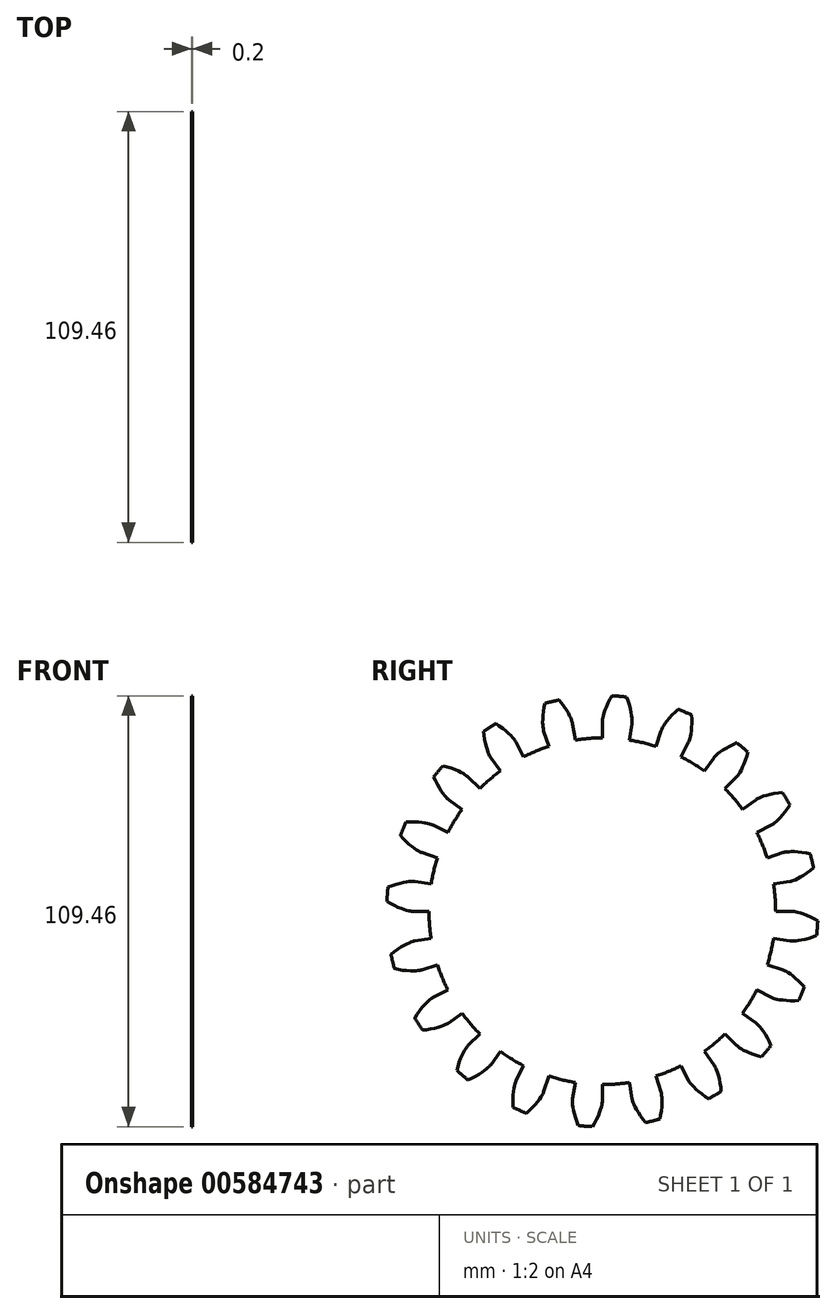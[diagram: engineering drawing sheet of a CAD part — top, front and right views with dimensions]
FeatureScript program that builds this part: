
annotation { "Feature Type Name" : "Feature", "Feature Type Description" : "" }
export const myFeature = defineFeature(function(context is Context, id is Id, definition is map)
    precondition{}
    {
        {
            assignVariable(context, id + "F0", {"name" : "GearThickness", "anyValue" : .2});
        }
        {
            var Q0;
            Q0=qCreatedBy(makeId("Right.planeOp"),FACE);
            var sketch = newSketch(context, id + "F1", { "sketchPlane" : qUnion([Q0])});
            skCircle(sketch, "E0", {"center": v(0, 0) * mm, "radius": 44.04 * mm});
            skCircle(sketch, "E1", {"center": v(0, 0) * mm, "radius": 48.22 * mm, "construction": true});
            skCircle(sketch, "E2", {"center": v(0, 0) * mm, "radius": 49.8 * mm, "construction": true});
            skCircle(sketch, "E3", {"center": v(0, 0) * mm, "radius": 54.78 * mm});
            skLineSegment(sketch, "E4", {"start": v(0, 0) * mm, "end": v(-48.22, 0) * mm, "construction": true});
            skLineSegment(sketch, "E5.1.0", {"start": v(0, 0) * mm, "end": v(-48.16, 2.4) * mm, "construction": true});
            skLineSegment(sketch, "E5.2.0", {"start": v(0, 0) * mm, "end": v(-47.98, 4.81) * mm, "construction": true});
            skLineSegment(sketch, "E5.3.0", {"start": v(0, 0) * mm, "end": v(-47.68, 7.2) * mm, "construction": true});
            skLineSegment(sketch, "E5.4.0", {"start": v(0, 0) * mm, "end": v(-47.26, 9.58) * mm, "construction": true});
            skLineSegment(sketch, "E5.5.0", {"start": v(0, 0) * mm, "end": v(-46.72, 11.93) * mm, "construction": true});
            skLineSegment(sketch, "E5.6.0", {"start": v(0, 0) * mm, "end": v(-46.06, 14.25) * mm, "construction": true});
            skLineSegment(sketch, "E5.7.0", {"start": v(0, 0) * mm, "end": v(-45.3, 16.53) * mm, "construction": true});
            skLineSegment(sketch, "E5.8.0", {"start": v(0, 0) * mm, "end": v(-44.41, 18.78) * mm, "construction": true});
            skLineSegment(sketch, "E5.9.0", {"start": v(0, 0) * mm, "end": v(-43.42, 20.97) * mm, "construction": true});
            skLineSegment(sketch, "E5.10.0", {"start": v(0, 0) * mm, "end": v(-42.31, 23.12) * mm, "construction": true});
            skLineSegment(sketch, "E5.11.0", {"start": v(0, 0) * mm, "end": v(-41.1, 25.2) * mm, "construction": true});
            skLineSegment(sketch, "E5.12.0", {"start": v(0, 0) * mm, "end": v(-39.8, 27.23) * mm, "construction": true});
            skLineSegment(sketch, "E5.13.0", {"start": v(0, 0) * mm, "end": v(-38.39, 29.18) * mm, "construction": true});
            skLineSegment(sketch, "E5.14.0", {"start": v(0, 0) * mm, "end": v(-36.88, 31.06) * mm, "construction": true});
            skLineSegment(sketch, "E5.anchor2", {"start": v(0, 0) * mm, "end": v(-36.88, 31.06) * mm, "construction": true});
            skLineSegment(sketch, "E6", {"start": v(-48.16, 2.4) * mm, "end": v(-48.28, 0) * mm, "construction": true});
            skLineSegment(sketch, "E7", {"start": v(-47.98, 4.81) * mm, "end": v(-48.46, 0.02) * mm, "construction": true});
            skLineSegment(sketch, "E8", {"start": v(-47.68, 7.2) * mm, "end": v(-48.76, 0.05) * mm, "construction": true});
            skLineSegment(sketch, "E9", {"start": v(-46.72, 11.93) * mm, "end": v(-49.7, 0.25) * mm, "construction": true});
            skLineSegment(sketch, "E10", {"start": v(-46.06, 14.25) * mm, "end": v(-50.34, 0.43) * mm, "construction": true});
            skLineSegment(sketch, "E11", {"start": v(-45.3, 16.53) * mm, "end": v(-51.08, 0.68) * mm, "construction": true});
            skLineSegment(sketch, "E12", {"start": v(-44.41, 18.78) * mm, "end": v(-51.92, 1.01) * mm, "construction": true});
            skLineSegment(sketch, "E13", {"start": v(-43.42, 20.97) * mm, "end": v(-52.86, 1.44) * mm, "construction": true});
            skLineSegment(sketch, "E14", {"start": v(-42.31, 23.12) * mm, "end": v(-53.87, 1.96) * mm, "construction": true});
            skLineSegment(sketch, "E15", {"start": v(-41.1, 25.2) * mm, "end": v(-54.97, 2.6) * mm, "construction": true});
            skLineSegment(sketch, "E16", {"start": v(-47.26, 9.58) * mm, "end": v(-49.17, 0.13) * mm, "construction": true});
            skLineSegment(sketch, "E17", {"start": v(-39.8, 27.23) * mm, "end": v(-56.13, 3.35) * mm, "construction": true});
            skLineSegment(sketch, "E18", {"start": v(-38.39, 29.18) * mm, "end": v(-57.35, 4.23) * mm, "construction": true});
            skLineSegment(sketch, "E19", {"start": v(-36.88, 31.06) * mm, "end": v(-58.62, 5.25) * mm, "construction": true});
            skLineSegment(sketch, "E20", {"start": v(0, 0) * mm, "end": v(-48.07, 3.78) * mm, "construction": true});
            skLineSegment(sketch, "E21", {"start": v(-44.04, 0) * mm, "end": v(-48.22, 0) * mm});
            skLineSegment(sketch, "E22.MirrorCS", {"start": v(-43.5, 6.89) * mm, "end": v(-47.62, 7.54) * mm});
            skLineSegment(sketch, "E23", {"start": v(-48.22, 0) * mm, "end": v(-48.28, 0) * mm});
            skLineSegment(sketch, "E24", {"start": v(-48.28, 0) * mm, "end": v(-48.46, 0.02) * mm});
            skLineSegment(sketch, "E25", {"start": v(-48.46, 0.02) * mm, "end": v(-48.76, 0.05) * mm});
            skLineSegment(sketch, "E26", {"start": v(-48.76, 0.05) * mm, "end": v(-49.17, 0.13) * mm});
            skLineSegment(sketch, "E27", {"start": v(-49.17, 0.13) * mm, "end": v(-49.7, 0.25) * mm});
            skLineSegment(sketch, "E28", {"start": v(-49.7, 0.25) * mm, "end": v(-50.34, 0.43) * mm});
            skLineSegment(sketch, "E29", {"start": v(-50.34, 0.43) * mm, "end": v(-51.08, 0.68) * mm});
            skLineSegment(sketch, "E30", {"start": v(-51.08, 0.68) * mm, "end": v(-51.92, 1.01) * mm});
            skLineSegment(sketch, "E31", {"start": v(-51.92, 1.01) * mm, "end": v(-52.86, 1.44) * mm});
            skLineSegment(sketch, "E32", {"start": v(-52.86, 1.44) * mm, "end": v(-53.87, 1.96) * mm});
            skLineSegment(sketch, "E33", {"start": v(-53.87, 1.96) * mm, "end": v(-54.97, 2.6) * mm});
            skLineSegment(sketch, "E34", {"start": v(-54.97, 2.6) * mm, "end": v(-56.13, 3.35) * mm});
            skLineSegment(sketch, "E35", {"start": v(-56.13, 3.35) * mm, "end": v(-57.35, 4.23) * mm});
            skLineSegment(sketch, "E36", {"start": v(-57.35, 4.23) * mm, "end": v(-58.62, 5.25) * mm});
            skLineSegment(sketch, "E37.MirrorCS", {"start": v(-47.62, 7.54) * mm, "end": v(-47.68, 7.55) * mm});
            skLineSegment(sketch, "E38.MirrorCS", {"start": v(-47.68, 7.55) * mm, "end": v(-47.86, 7.56) * mm});
            skLineSegment(sketch, "E39.MirrorCS", {"start": v(-47.86, 7.56) * mm, "end": v(-48.17, 7.57) * mm});
            skLineSegment(sketch, "E40.MirrorCS", {"start": v(-48.17, 7.57) * mm, "end": v(-48.59, 7.57) * mm});
            skLineSegment(sketch, "E41.MirrorCS", {"start": v(-49.13, 7.53) * mm, "end": v(-49.79, 7.45) * mm});
            skLineSegment(sketch, "E42.MirrorCS", {"start": v(-49.79, 7.45) * mm, "end": v(-50.56, 7.32) * mm});
            skLineSegment(sketch, "E43.MirrorCS", {"start": v(-50.56, 7.32) * mm, "end": v(-51.44, 7.12) * mm});
            skLineSegment(sketch, "E44.MirrorCS", {"start": v(-51.44, 7.12) * mm, "end": v(-52.43, 6.85) * mm});
            skLineSegment(sketch, "E45.MirrorCS", {"start": v(-53.52, 6.5) * mm, "end": v(-54.7, 6.04) * mm});
            skLineSegment(sketch, "E46.MirrorCS", {"start": v(-52.43, 6.85) * mm, "end": v(-53.52, 6.5) * mm});
            skLineSegment(sketch, "E47.MirrorCS", {"start": v(-54.7, 6.04) * mm, "end": v(-55.96, 5.47) * mm});
            skLineSegment(sketch, "E48.MirrorCS", {"start": v(-55.96, 5.47) * mm, "end": v(-57.3, 4.8) * mm});
            skLineSegment(sketch, "E49.MirrorCS", {"start": v(-57.3, 4.8) * mm, "end": v(-58.72, 3.99) * mm});
            skLineSegment(sketch, "E50.MirrorCS", {"start": v(-48.59, 7.57) * mm, "end": v(-49.13, 7.53) * mm});
            skLineSegment(sketch, "E51.1.0", {"start": v(-41.89, -13.6) * mm, "end": v(-45.86, -14.9) * mm});
            skLineSegment(sketch, "E51.1.1", {"start": v(-53.89, -11.16) * mm, "end": v(-54.92, -12.09) * mm});
            skLineSegment(sketch, "E51.1.2", {"start": v(-43.5, -6.89) * mm, "end": v(-47.62, -7.54) * mm});
            skLineSegment(sketch, "E51.1.3", {"start": v(-52.9, -10.36) * mm, "end": v(-53.89, -11.16) * mm});
            skLineSegment(sketch, "E51.1.4", {"start": v(-51.84, -14.78) * mm, "end": v(-53.08, -14.52) * mm});
            skLineSegment(sketch, "E51.1.5", {"start": v(-53.08, -14.52) * mm, "end": v(-54.42, -14.16) * mm});
            skLineSegment(sketch, "E51.1.6", {"start": v(-51.98, -9.69) * mm, "end": v(-52.9, -10.36) * mm});
            skLineSegment(sketch, "E51.1.7", {"start": v(-55.98, -13.15) * mm, "end": v(-57.08, -14.35) * mm});
            skLineSegment(sketch, "E51.1.8", {"start": v(-51.12, -9.12) * mm, "end": v(-51.98, -9.69) * mm});
            skLineSegment(sketch, "E51.1.9", {"start": v(-55.85, -13.7) * mm, "end": v(-57.37, -13.12) * mm});
            skLineSegment(sketch, "E51.1.10", {"start": v(-54.92, -12.09) * mm, "end": v(-55.98, -13.15) * mm});
            skLineSegment(sketch, "E51.1.11", {"start": v(-50.71, -14.97) * mm, "end": v(-51.84, -14.78) * mm});
            skLineSegment(sketch, "E51.1.12", {"start": v(-54.42, -14.16) * mm, "end": v(-55.85, -13.7) * mm});
            skLineSegment(sketch, "E51.1.13", {"start": v(-49.05, -8.02) * mm, "end": v(-49.65, -8.3) * mm});
            skLineSegment(sketch, "E51.1.14", {"start": v(-49.65, -8.3) * mm, "end": v(-50.35, -8.66) * mm});
            skLineSegment(sketch, "E51.1.15", {"start": v(-50.35, -8.66) * mm, "end": v(-51.12, -9.12) * mm});
            skLineSegment(sketch, "E51.1.16", {"start": v(-48.8, -15.14) * mm, "end": v(-49.7, -15.08) * mm});
            skLineSegment(sketch, "E51.1.17", {"start": v(-48, -15.15) * mm, "end": v(-48.8, -15.14) * mm});
            skLineSegment(sketch, "E51.1.18", {"start": v(-49.7, -15.08) * mm, "end": v(-50.71, -14.97) * mm});
            skLineSegment(sketch, "E51.1.19", {"start": v(-48.55, -7.82) * mm, "end": v(-49.05, -8.02) * mm});
            skLineSegment(sketch, "E51.1.20", {"start": v(-48.15, -7.68) * mm, "end": v(-48.55, -7.82) * mm});
            skLineSegment(sketch, "E51.1.21", {"start": v(-47.35, -15.12) * mm, "end": v(-48, -15.15) * mm});
            skLineSegment(sketch, "E51.1.22", {"start": v(-46.8, -15.07) * mm, "end": v(-47.35, -15.12) * mm});
            skLineSegment(sketch, "E51.1.23", {"start": v(-46.1, -14.96) * mm, "end": v(-46.39, -15.02) * mm});
            skLineSegment(sketch, "E51.1.24", {"start": v(-47.62, -7.54) * mm, "end": v(-47.68, -7.55) * mm});
            skLineSegment(sketch, "E51.1.25", {"start": v(-47.68, -7.55) * mm, "end": v(-47.86, -7.6) * mm});
            skLineSegment(sketch, "E51.1.26", {"start": v(-46.39, -15.02) * mm, "end": v(-46.8, -15.07) * mm});
            skLineSegment(sketch, "E51.1.27", {"start": v(-47.86, -7.6) * mm, "end": v(-48.15, -7.68) * mm});
            skLineSegment(sketch, "E51.1.28", {"start": v(-45.92, -14.92) * mm, "end": v(-46.1, -14.96) * mm});
            skLineSegment(sketch, "E51.1.29", {"start": v(-45.86, -14.9) * mm, "end": v(-45.92, -14.92) * mm});
            skLineSegment(sketch, "E51.2.0", {"start": v(-35.63, -25.89) * mm, "end": v(-39, -28.34) * mm});
            skLineSegment(sketch, "E51.2.1", {"start": v(-47.8, -27.27) * mm, "end": v(-48.5, -28.47) * mm});
            skLineSegment(sketch, "E51.2.2", {"start": v(-39.24, -20) * mm, "end": v(-42.96, -21.9) * mm});
            skLineSegment(sketch, "E51.2.3", {"start": v(-47.11, -26.2) * mm, "end": v(-47.8, -27.27) * mm});
            skLineSegment(sketch, "E51.2.4", {"start": v(-44.74, -30.08) * mm, "end": v(-46, -30.21) * mm});
            skLineSegment(sketch, "E51.2.5", {"start": v(-46, -30.21) * mm, "end": v(-47.38, -30.28) * mm});
            skLineSegment(sketch, "E51.2.6", {"start": v(-46.44, -25.27) * mm, "end": v(-47.11, -26.2) * mm});
            skLineSegment(sketch, "E51.2.7", {"start": v(-49.18, -29.8) * mm, "end": v(-49.85, -31.29) * mm});
            skLineSegment(sketch, "E51.2.8", {"start": v(-45.8, -24.47) * mm, "end": v(-46.44, -25.27) * mm});
            skLineSegment(sketch, "E51.2.9", {"start": v(-48.89, -30.29) * mm, "end": v(-50.51, -30.21) * mm});
            skLineSegment(sketch, "E51.2.10", {"start": v(-48.5, -28.47) * mm, "end": v(-49.18, -29.8) * mm});
            skLineSegment(sketch, "E51.2.11", {"start": v(-43.6, -29.9) * mm, "end": v(-44.74, -30.08) * mm});
            skLineSegment(sketch, "E51.2.12", {"start": v(-47.38, -30.28) * mm, "end": v(-48.89, -30.29) * mm});
            skLineSegment(sketch, "E51.2.13", {"start": v(-44.17, -22.79) * mm, "end": v(-44.66, -23.24) * mm});
            skLineSegment(sketch, "E51.2.14", {"start": v(-44.66, -23.24) * mm, "end": v(-45.2, -23.8) * mm});
            skLineSegment(sketch, "E51.2.15", {"start": v(-45.2, -23.8) * mm, "end": v(-45.8, -24.47) * mm});
            skLineSegment(sketch, "E51.2.16", {"start": v(-41.73, -29.47) * mm, "end": v(-42.6, -29.7) * mm});
            skLineSegment(sketch, "E51.2.17", {"start": v(-40.98, -29.24) * mm, "end": v(-41.73, -29.47) * mm});
            skLineSegment(sketch, "E51.2.18", {"start": v(-42.6, -29.7) * mm, "end": v(-43.6, -29.9) * mm});
            skLineSegment(sketch, "E51.2.19", {"start": v(-43.75, -22.44) * mm, "end": v(-44.17, -22.79) * mm});
            skLineSegment(sketch, "E51.2.20", {"start": v(-43.42, -22.18) * mm, "end": v(-43.75, -22.44) * mm});
            skLineSegment(sketch, "E51.2.21", {"start": v(-40.36, -29.01) * mm, "end": v(-40.98, -29.24) * mm});
            skLineSegment(sketch, "E51.2.22", {"start": v(-39.86, -28.8) * mm, "end": v(-40.36, -29.01) * mm});
            skLineSegment(sketch, "E51.2.23", {"start": v(-39.21, -28.47) * mm, "end": v(-39.48, -28.61) * mm});
            skLineSegment(sketch, "E51.2.24", {"start": v(-42.96, -21.9) * mm, "end": v(-43.01, -21.92) * mm});
            skLineSegment(sketch, "E51.2.25", {"start": v(-43.01, -21.92) * mm, "end": v(-43.17, -22.01) * mm});
            skLineSegment(sketch, "E51.2.26", {"start": v(-39.48, -28.61) * mm, "end": v(-39.86, -28.8) * mm});
            skLineSegment(sketch, "E51.2.27", {"start": v(-43.17, -22.01) * mm, "end": v(-43.42, -22.18) * mm});
            skLineSegment(sketch, "E51.2.28", {"start": v(-39.06, -28.38) * mm, "end": v(-39.21, -28.47) * mm});
            skLineSegment(sketch, "E51.2.29", {"start": v(-39, -28.34) * mm, "end": v(-39.06, -28.38) * mm});
            skLineSegment(sketch, "E51.3.0", {"start": v(-25.89, -35.63) * mm, "end": v(-28.34, -39) * mm});
            skLineSegment(sketch, "E51.3.1", {"start": v(-37.03, -40.7) * mm, "end": v(-37.32, -42.06) * mm});
            skLineSegment(sketch, "E51.3.2", {"start": v(-31.14, -31.14) * mm, "end": v(-34.1, -34.1) * mm});
            skLineSegment(sketch, "E51.3.3", {"start": v(-36.7, -39.48) * mm, "end": v(-37.03, -40.7) * mm});
            skLineSegment(sketch, "E51.3.4", {"start": v(-33.25, -42.43) * mm, "end": v(-34.4, -42.95) * mm});
            skLineSegment(sketch, "E51.3.5", {"start": v(-34.4, -42.95) * mm, "end": v(-35.7, -43.44) * mm});
            skLineSegment(sketch, "E51.3.6", {"start": v(-36.36, -38.39) * mm, "end": v(-36.7, -39.48) * mm});
            skLineSegment(sketch, "E51.3.7", {"start": v(-37.56, -43.55) * mm, "end": v(-37.74, -45.16) * mm});
            skLineSegment(sketch, "E51.3.8", {"start": v(-36, -37.43) * mm, "end": v(-36.36, -38.39) * mm});
            skLineSegment(sketch, "E51.3.9", {"start": v(-37.13, -43.91) * mm, "end": v(-38.7, -44.34) * mm});
            skLineSegment(sketch, "E51.3.10", {"start": v(-37.32, -42.06) * mm, "end": v(-37.56, -43.55) * mm});
            skLineSegment(sketch, "E51.3.11", {"start": v(-32.23, -41.92) * mm, "end": v(-33.25, -42.43) * mm});
            skLineSegment(sketch, "E51.3.12", {"start": v(-35.7, -43.44) * mm, "end": v(-37.13, -43.91) * mm});
            skLineSegment(sketch, "E51.3.13", {"start": v(-34.97, -35.32) * mm, "end": v(-35.3, -35.9) * mm});
            skLineSegment(sketch, "E51.3.14", {"start": v(-35.3, -35.9) * mm, "end": v(-35.64, -36.6) * mm});
            skLineSegment(sketch, "E51.3.15", {"start": v(-35.64, -36.6) * mm, "end": v(-36, -37.43) * mm});
            skLineSegment(sketch, "E51.3.16", {"start": v(-30.58, -40.93) * mm, "end": v(-31.34, -41.41) * mm});
            skLineSegment(sketch, "E51.3.17", {"start": v(-29.94, -40.47) * mm, "end": v(-30.58, -40.93) * mm});
            skLineSegment(sketch, "E51.3.18", {"start": v(-31.34, -41.41) * mm, "end": v(-32.23, -41.92) * mm});
            skLineSegment(sketch, "E51.3.19", {"start": v(-34.68, -34.86) * mm, "end": v(-34.97, -35.32) * mm});
            skLineSegment(sketch, "E51.3.20", {"start": v(-34.44, -34.51) * mm, "end": v(-34.68, -34.86) * mm});
            skLineSegment(sketch, "E51.3.21", {"start": v(-29.42, -40.06) * mm, "end": v(-29.94, -40.47) * mm});
            skLineSegment(sketch, "E51.3.22", {"start": v(-29, -39.7) * mm, "end": v(-29.42, -40.06) * mm});
            skLineSegment(sketch, "E51.3.23", {"start": v(-28.5, -39.2) * mm, "end": v(-28.7, -39.41) * mm});
            skLineSegment(sketch, "E51.3.24", {"start": v(-34.1, -34.1) * mm, "end": v(-34.14, -34.14) * mm});
            skLineSegment(sketch, "E51.3.25", {"start": v(-34.14, -34.14) * mm, "end": v(-34.25, -34.28) * mm});
            skLineSegment(sketch, "E51.3.26", {"start": v(-28.7, -39.41) * mm, "end": v(-29, -39.7) * mm});
            skLineSegment(sketch, "E51.3.27", {"start": v(-34.25, -34.28) * mm, "end": v(-34.44, -34.51) * mm});
            skLineSegment(sketch, "E51.3.28", {"start": v(-28.38, -39.06) * mm, "end": v(-28.5, -39.2) * mm});
            skLineSegment(sketch, "E51.3.29", {"start": v(-28.34, -39) * mm, "end": v(-28.38, -39.06) * mm});
            skLineSegment(sketch, "E51.4.0", {"start": v(-13.6, -41.89) * mm, "end": v(-14.9, -45.86) * mm});
            skLineSegment(sketch, "E51.4.1", {"start": v(-22.64, -50.15) * mm, "end": v(-22.5, -51.53) * mm});
            skLineSegment(sketch, "E51.4.2", {"start": v(-20, -39.24) * mm, "end": v(-21.9, -42.96) * mm});
            skLineSegment(sketch, "E51.4.3", {"start": v(-22.71, -48.9) * mm, "end": v(-22.64, -50.15) * mm});
            skLineSegment(sketch, "E51.4.4", {"start": v(-18.51, -50.63) * mm, "end": v(-19.45, -51.48) * mm});
            skLineSegment(sketch, "E51.4.5", {"start": v(-19.45, -51.48) * mm, "end": v(-20.53, -52.35) * mm});
            skLineSegment(sketch, "E51.4.6", {"start": v(-22.72, -47.75) * mm, "end": v(-22.71, -48.9) * mm});
            skLineSegment(sketch, "E51.4.7", {"start": v(-22.27, -53.02) * mm, "end": v(-21.94, -54.62) * mm});
            skLineSegment(sketch, "E51.4.8", {"start": v(-22.67, -46.72) * mm, "end": v(-22.72, -47.75) * mm});
            skLineSegment(sketch, "E51.4.9", {"start": v(-21.75, -53.24) * mm, "end": v(-23.1, -54.13) * mm});
            skLineSegment(sketch, "E51.4.10", {"start": v(-22.5, -51.53) * mm, "end": v(-22.27, -53.02) * mm});
            skLineSegment(sketch, "E51.4.11", {"start": v(-17.7, -49.82) * mm, "end": v(-18.51, -50.63) * mm});
            skLineSegment(sketch, "E51.4.12", {"start": v(-20.53, -52.35) * mm, "end": v(-21.75, -53.24) * mm});
            skLineSegment(sketch, "E51.4.13", {"start": v(-22.34, -44.4) * mm, "end": v(-22.47, -45.05) * mm});
            skLineSegment(sketch, "E51.4.14", {"start": v(-22.47, -45.05) * mm, "end": v(-22.58, -45.82) * mm});
            skLineSegment(sketch, "E51.4.15", {"start": v(-22.58, -45.82) * mm, "end": v(-22.67, -46.72) * mm});
            skLineSegment(sketch, "E51.4.16", {"start": v(-16.43, -48.37) * mm, "end": v(-17, -49.07) * mm});
            skLineSegment(sketch, "E51.4.17", {"start": v(-15.96, -47.74) * mm, "end": v(-16.43, -48.37) * mm});
            skLineSegment(sketch, "E51.4.18", {"start": v(-17, -49.07) * mm, "end": v(-17.7, -49.82) * mm});
            skLineSegment(sketch, "E51.4.19", {"start": v(-22.2, -43.87) * mm, "end": v(-22.34, -44.4) * mm});
            skLineSegment(sketch, "E51.4.20", {"start": v(-22.09, -43.47) * mm, "end": v(-22.2, -43.87) * mm});
            skLineSegment(sketch, "E51.4.21", {"start": v(-15.6, -47.2) * mm, "end": v(-15.96, -47.74) * mm});
            skLineSegment(sketch, "E51.4.22", {"start": v(-15.32, -46.73) * mm, "end": v(-15.6, -47.2) * mm});
            skLineSegment(sketch, "E51.4.23", {"start": v(-14.99, -46.08) * mm, "end": v(-15.12, -46.35) * mm});
            skLineSegment(sketch, "E51.4.24", {"start": v(-21.9, -42.96) * mm, "end": v(-21.92, -43.02) * mm});
            skLineSegment(sketch, "E51.4.25", {"start": v(-21.92, -43.02) * mm, "end": v(-21.99, -43.18) * mm});
            skLineSegment(sketch, "E51.4.26", {"start": v(-15.12, -46.35) * mm, "end": v(-15.32, -46.73) * mm});
            skLineSegment(sketch, "E51.4.27", {"start": v(-21.99, -43.18) * mm, "end": v(-22.09, -43.47) * mm});
            skLineSegment(sketch, "E51.4.28", {"start": v(-14.92, -45.91) * mm, "end": v(-14.99, -46.08) * mm});
            skLineSegment(sketch, "E51.4.29", {"start": v(-14.9, -45.86) * mm, "end": v(-14.92, -45.91) * mm});
            skLineSegment(sketch, "E51.5.0", {"start": v(0, -44.04) * mm, "end": v(0, -48.22) * mm});
            skLineSegment(sketch, "E51.5.1", {"start": v(-6.04, -54.7) * mm, "end": v(-5.47, -55.96) * mm});
            skLineSegment(sketch, "E51.5.2", {"start": v(-6.89, -43.5) * mm, "end": v(-7.54, -47.62) * mm});
            skLineSegment(sketch, "E51.5.3", {"start": v(-6.5, -53.52) * mm, "end": v(-6.04, -54.7) * mm});
            skLineSegment(sketch, "E51.5.4", {"start": v(-1.96, -53.87) * mm, "end": v(-2.6, -54.97) * mm});
            skLineSegment(sketch, "E51.5.5", {"start": v(-2.6, -54.97) * mm, "end": v(-3.35, -56.13) * mm});
            skLineSegment(sketch, "E51.5.6", {"start": v(-6.85, -52.43) * mm, "end": v(-6.5, -53.52) * mm});
            skLineSegment(sketch, "E51.5.7", {"start": v(-4.8, -57.3) * mm, "end": v(-3.99, -58.72) * mm});
            skLineSegment(sketch, "E51.5.8", {"start": v(-7.12, -51.44) * mm, "end": v(-6.85, -52.43) * mm});
            skLineSegment(sketch, "E51.5.9", {"start": v(-4.23, -57.35) * mm, "end": v(-5.25, -58.62) * mm});
            skLineSegment(sketch, "E51.5.10", {"start": v(-5.47, -55.96) * mm, "end": v(-4.8, -57.3) * mm});
            skLineSegment(sketch, "E51.5.11", {"start": v(-1.44, -52.86) * mm, "end": v(-1.96, -53.87) * mm});
            skLineSegment(sketch, "E51.5.12", {"start": v(-3.35, -56.13) * mm, "end": v(-4.23, -57.35) * mm});
            skLineSegment(sketch, "E51.5.13", {"start": v(-7.53, -49.13) * mm, "end": v(-7.45, -49.79) * mm});
            skLineSegment(sketch, "E51.5.14", {"start": v(-7.45, -49.79) * mm, "end": v(-7.32, -50.56) * mm});
            skLineSegment(sketch, "E51.5.15", {"start": v(-7.32, -50.56) * mm, "end": v(-7.12, -51.44) * mm});
            skLineSegment(sketch, "E51.5.16", {"start": v(-0.68, -51.08) * mm, "end": v(-1.01, -51.92) * mm});
            skLineSegment(sketch, "E51.5.17", {"start": v(-0.43, -50.34) * mm, "end": v(-0.68, -51.08) * mm});
            skLineSegment(sketch, "E51.5.18", {"start": v(-1.01, -51.92) * mm, "end": v(-1.44, -52.86) * mm});
            skLineSegment(sketch, "E51.5.19", {"start": v(-7.57, -48.59) * mm, "end": v(-7.53, -49.13) * mm});
            skLineSegment(sketch, "E51.5.20", {"start": v(-7.57, -48.17) * mm, "end": v(-7.57, -48.59) * mm});
            skLineSegment(sketch, "E51.5.21", {"start": v(-0.25, -49.7) * mm, "end": v(-0.43, -50.34) * mm});
            skLineSegment(sketch, "E51.5.22", {"start": v(-0.13, -49.17) * mm, "end": v(-0.25, -49.7) * mm});
            skLineSegment(sketch, "E51.5.23", {"start": v(-0.02, -48.46) * mm, "end": v(-0.05, -48.76) * mm});
            skLineSegment(sketch, "E51.5.24", {"start": v(-7.54, -47.62) * mm, "end": v(-7.55, -47.68) * mm});
            skLineSegment(sketch, "E51.5.25", {"start": v(-7.55, -47.68) * mm, "end": v(-7.56, -47.86) * mm});
            skLineSegment(sketch, "E51.5.26", {"start": v(-0.05, -48.76) * mm, "end": v(-0.13, -49.17) * mm});
            skLineSegment(sketch, "E51.5.27", {"start": v(-7.56, -47.86) * mm, "end": v(-7.57, -48.17) * mm});
            skLineSegment(sketch, "E51.5.28", {"start": v(0, -48.28) * mm, "end": v(-0.02, -48.46) * mm});
            skLineSegment(sketch, "E51.5.29", {"start": v(0, -48.22) * mm, "end": v(0, -48.28) * mm});
            skLineSegment(sketch, "E51.6.0", {"start": v(13.6, -41.89) * mm, "end": v(14.9, -45.86) * mm});
            skLineSegment(sketch, "E51.6.1", {"start": v(11.16, -53.89) * mm, "end": v(12.09, -54.92) * mm});
            skLineSegment(sketch, "E51.6.2", {"start": v(6.89, -43.5) * mm, "end": v(7.54, -47.62) * mm});
            skLineSegment(sketch, "E51.6.3", {"start": v(10.36, -52.9) * mm, "end": v(11.16, -53.89) * mm});
            skLineSegment(sketch, "E51.6.4", {"start": v(14.78, -51.84) * mm, "end": v(14.52, -53.08) * mm});
            skLineSegment(sketch, "E51.6.5", {"start": v(14.52, -53.08) * mm, "end": v(14.16, -54.42) * mm});
            skLineSegment(sketch, "E51.6.6", {"start": v(9.69, -51.98) * mm, "end": v(10.36, -52.9) * mm});
            skLineSegment(sketch, "E51.6.7", {"start": v(13.15, -55.98) * mm, "end": v(14.35, -57.08) * mm});
            skLineSegment(sketch, "E51.6.8", {"start": v(9.12, -51.12) * mm, "end": v(9.69, -51.98) * mm});
            skLineSegment(sketch, "E51.6.9", {"start": v(13.7, -55.85) * mm, "end": v(13.12, -57.37) * mm});
            skLineSegment(sketch, "E51.6.10", {"start": v(12.09, -54.92) * mm, "end": v(13.15, -55.98) * mm});
            skLineSegment(sketch, "E51.6.11", {"start": v(14.97, -50.71) * mm, "end": v(14.78, -51.84) * mm});
            skLineSegment(sketch, "E51.6.12", {"start": v(14.16, -54.42) * mm, "end": v(13.7, -55.85) * mm});
            skLineSegment(sketch, "E51.6.13", {"start": v(8.02, -49.05) * mm, "end": v(8.3, -49.65) * mm});
            skLineSegment(sketch, "E51.6.14", {"start": v(8.3, -49.65) * mm, "end": v(8.66, -50.35) * mm});
            skLineSegment(sketch, "E51.6.15", {"start": v(8.66, -50.35) * mm, "end": v(9.12, -51.12) * mm});
            skLineSegment(sketch, "E51.6.16", {"start": v(15.14, -48.8) * mm, "end": v(15.08, -49.7) * mm});
            skLineSegment(sketch, "E51.6.17", {"start": v(15.15, -48) * mm, "end": v(15.14, -48.8) * mm});
            skLineSegment(sketch, "E51.6.18", {"start": v(15.08, -49.7) * mm, "end": v(14.97, -50.71) * mm});
            skLineSegment(sketch, "E51.6.19", {"start": v(7.82, -48.55) * mm, "end": v(8.02, -49.05) * mm});
            skLineSegment(sketch, "E51.6.20", {"start": v(7.68, -48.15) * mm, "end": v(7.82, -48.55) * mm});
            skLineSegment(sketch, "E51.6.21", {"start": v(15.12, -47.35) * mm, "end": v(15.15, -48) * mm});
            skLineSegment(sketch, "E51.6.22", {"start": v(15.07, -46.8) * mm, "end": v(15.12, -47.35) * mm});
            skLineSegment(sketch, "E51.6.23", {"start": v(14.96, -46.1) * mm, "end": v(15.02, -46.39) * mm});
            skLineSegment(sketch, "E51.6.24", {"start": v(7.54, -47.62) * mm, "end": v(7.55, -47.68) * mm});
            skLineSegment(sketch, "E51.6.25", {"start": v(7.55, -47.68) * mm, "end": v(7.6, -47.86) * mm});
            skLineSegment(sketch, "E51.6.26", {"start": v(15.02, -46.39) * mm, "end": v(15.07, -46.8) * mm});
            skLineSegment(sketch, "E51.6.27", {"start": v(7.6, -47.86) * mm, "end": v(7.68, -48.15) * mm});
            skLineSegment(sketch, "E51.6.28", {"start": v(14.92, -45.92) * mm, "end": v(14.96, -46.1) * mm});
            skLineSegment(sketch, "E51.6.29", {"start": v(14.9, -45.86) * mm, "end": v(14.92, -45.92) * mm});
            skLineSegment(sketch, "E51.7.0", {"start": v(25.89, -35.63) * mm, "end": v(28.34, -39) * mm});
            skLineSegment(sketch, "E51.7.1", {"start": v(27.27, -47.8) * mm, "end": v(28.47, -48.5) * mm});
            skLineSegment(sketch, "E51.7.2", {"start": v(20, -39.24) * mm, "end": v(21.9, -42.96) * mm});
            skLineSegment(sketch, "E51.7.3", {"start": v(26.2, -47.11) * mm, "end": v(27.27, -47.8) * mm});
            skLineSegment(sketch, "E51.7.4", {"start": v(30.08, -44.74) * mm, "end": v(30.21, -46) * mm});
            skLineSegment(sketch, "E51.7.5", {"start": v(30.21, -46) * mm, "end": v(30.28, -47.38) * mm});
            skLineSegment(sketch, "E51.7.6", {"start": v(25.27, -46.44) * mm, "end": v(26.2, -47.11) * mm});
            skLineSegment(sketch, "E51.7.7", {"start": v(29.8, -49.18) * mm, "end": v(31.29, -49.85) * mm});
            skLineSegment(sketch, "E51.7.8", {"start": v(24.47, -45.8) * mm, "end": v(25.27, -46.44) * mm});
            skLineSegment(sketch, "E51.7.9", {"start": v(30.29, -48.89) * mm, "end": v(30.21, -50.51) * mm});
            skLineSegment(sketch, "E51.7.10", {"start": v(28.47, -48.5) * mm, "end": v(29.8, -49.18) * mm});
            skLineSegment(sketch, "E51.7.11", {"start": v(29.9, -43.6) * mm, "end": v(30.08, -44.74) * mm});
            skLineSegment(sketch, "E51.7.12", {"start": v(30.28, -47.38) * mm, "end": v(30.29, -48.89) * mm});
            skLineSegment(sketch, "E51.7.13", {"start": v(22.79, -44.17) * mm, "end": v(23.24, -44.66) * mm});
            skLineSegment(sketch, "E51.7.14", {"start": v(23.24, -44.66) * mm, "end": v(23.8, -45.2) * mm});
            skLineSegment(sketch, "E51.7.15", {"start": v(23.8, -45.2) * mm, "end": v(24.47, -45.8) * mm});
            skLineSegment(sketch, "E51.7.16", {"start": v(29.47, -41.73) * mm, "end": v(29.7, -42.6) * mm});
            skLineSegment(sketch, "E51.7.17", {"start": v(29.24, -40.98) * mm, "end": v(29.47, -41.73) * mm});
            skLineSegment(sketch, "E51.7.18", {"start": v(29.7, -42.6) * mm, "end": v(29.9, -43.6) * mm});
            skLineSegment(sketch, "E51.7.19", {"start": v(22.44, -43.75) * mm, "end": v(22.79, -44.17) * mm});
            skLineSegment(sketch, "E51.7.20", {"start": v(22.18, -43.42) * mm, "end": v(22.44, -43.75) * mm});
            skLineSegment(sketch, "E51.7.21", {"start": v(29.01, -40.36) * mm, "end": v(29.24, -40.98) * mm});
            skLineSegment(sketch, "E51.7.22", {"start": v(28.8, -39.86) * mm, "end": v(29.01, -40.36) * mm});
            skLineSegment(sketch, "E51.7.23", {"start": v(28.47, -39.21) * mm, "end": v(28.61, -39.48) * mm});
            skLineSegment(sketch, "E51.7.24", {"start": v(21.9, -42.96) * mm, "end": v(21.92, -43.01) * mm});
            skLineSegment(sketch, "E51.7.25", {"start": v(21.92, -43.01) * mm, "end": v(22.01, -43.17) * mm});
            skLineSegment(sketch, "E51.7.26", {"start": v(28.61, -39.48) * mm, "end": v(28.8, -39.86) * mm});
            skLineSegment(sketch, "E51.7.27", {"start": v(22.01, -43.17) * mm, "end": v(22.18, -43.42) * mm});
            skLineSegment(sketch, "E51.7.28", {"start": v(28.38, -39.06) * mm, "end": v(28.47, -39.21) * mm});
            skLineSegment(sketch, "E51.7.29", {"start": v(28.34, -39) * mm, "end": v(28.38, -39.06) * mm});
            skLineSegment(sketch, "E51.8.0", {"start": v(35.63, -25.89) * mm, "end": v(39, -28.34) * mm});
            skLineSegment(sketch, "E51.8.1", {"start": v(40.7, -37.03) * mm, "end": v(42.06, -37.32) * mm});
            skLineSegment(sketch, "E51.8.2", {"start": v(31.14, -31.14) * mm, "end": v(34.1, -34.1) * mm});
            skLineSegment(sketch, "E51.8.3", {"start": v(39.48, -36.7) * mm, "end": v(40.7, -37.03) * mm});
            skLineSegment(sketch, "E51.8.4", {"start": v(42.43, -33.25) * mm, "end": v(42.95, -34.4) * mm});
            skLineSegment(sketch, "E51.8.5", {"start": v(42.95, -34.4) * mm, "end": v(43.44, -35.7) * mm});
            skLineSegment(sketch, "E51.8.6", {"start": v(38.39, -36.36) * mm, "end": v(39.48, -36.7) * mm});
            skLineSegment(sketch, "E51.8.7", {"start": v(43.55, -37.56) * mm, "end": v(45.16, -37.74) * mm});
            skLineSegment(sketch, "E51.8.8", {"start": v(37.43, -36) * mm, "end": v(38.39, -36.36) * mm});
            skLineSegment(sketch, "E51.8.9", {"start": v(43.91, -37.13) * mm, "end": v(44.34, -38.7) * mm});
            skLineSegment(sketch, "E51.8.10", {"start": v(42.06, -37.32) * mm, "end": v(43.55, -37.56) * mm});
            skLineSegment(sketch, "E51.8.11", {"start": v(41.92, -32.23) * mm, "end": v(42.43, -33.25) * mm});
            skLineSegment(sketch, "E51.8.12", {"start": v(43.44, -35.7) * mm, "end": v(43.91, -37.13) * mm});
            skLineSegment(sketch, "E51.8.13", {"start": v(35.32, -34.97) * mm, "end": v(35.9, -35.3) * mm});
            skLineSegment(sketch, "E51.8.14", {"start": v(35.9, -35.3) * mm, "end": v(36.6, -35.64) * mm});
            skLineSegment(sketch, "E51.8.15", {"start": v(36.6, -35.64) * mm, "end": v(37.43, -36) * mm});
            skLineSegment(sketch, "E51.8.16", {"start": v(40.93, -30.58) * mm, "end": v(41.41, -31.34) * mm});
            skLineSegment(sketch, "E51.8.17", {"start": v(40.47, -29.94) * mm, "end": v(40.93, -30.58) * mm});
            skLineSegment(sketch, "E51.8.18", {"start": v(41.41, -31.34) * mm, "end": v(41.92, -32.23) * mm});
            skLineSegment(sketch, "E51.8.19", {"start": v(34.86, -34.68) * mm, "end": v(35.32, -34.97) * mm});
            skLineSegment(sketch, "E51.8.20", {"start": v(34.51, -34.44) * mm, "end": v(34.86, -34.68) * mm});
            skLineSegment(sketch, "E51.8.21", {"start": v(40.06, -29.42) * mm, "end": v(40.47, -29.94) * mm});
            skLineSegment(sketch, "E51.8.22", {"start": v(39.7, -29) * mm, "end": v(40.06, -29.42) * mm});
            skLineSegment(sketch, "E51.8.23", {"start": v(39.2, -28.5) * mm, "end": v(39.41, -28.7) * mm});
            skLineSegment(sketch, "E51.8.24", {"start": v(34.1, -34.1) * mm, "end": v(34.14, -34.14) * mm});
            skLineSegment(sketch, "E51.8.25", {"start": v(34.14, -34.14) * mm, "end": v(34.28, -34.25) * mm});
            skLineSegment(sketch, "E51.8.26", {"start": v(39.41, -28.7) * mm, "end": v(39.7, -29) * mm});
            skLineSegment(sketch, "E51.8.27", {"start": v(34.28, -34.25) * mm, "end": v(34.51, -34.44) * mm});
            skLineSegment(sketch, "E51.8.28", {"start": v(39.06, -28.38) * mm, "end": v(39.2, -28.5) * mm});
            skLineSegment(sketch, "E51.8.29", {"start": v(39, -28.34) * mm, "end": v(39.06, -28.38) * mm});
            skLineSegment(sketch, "E51.9.0", {"start": v(41.89, -13.6) * mm, "end": v(45.86, -14.9) * mm});
            skLineSegment(sketch, "E51.9.1", {"start": v(50.15, -22.64) * mm, "end": v(51.53, -22.5) * mm});
            skLineSegment(sketch, "E51.9.2", {"start": v(39.24, -20) * mm, "end": v(42.96, -21.9) * mm});
            skLineSegment(sketch, "E51.9.3", {"start": v(48.9, -22.71) * mm, "end": v(50.15, -22.64) * mm});
            skLineSegment(sketch, "E51.9.4", {"start": v(50.63, -18.51) * mm, "end": v(51.48, -19.45) * mm});
            skLineSegment(sketch, "E51.9.5", {"start": v(51.48, -19.45) * mm, "end": v(52.35, -20.53) * mm});
            skLineSegment(sketch, "E51.9.6", {"start": v(47.75, -22.72) * mm, "end": v(48.9, -22.71) * mm});
            skLineSegment(sketch, "E51.9.7", {"start": v(53.02, -22.27) * mm, "end": v(54.62, -21.94) * mm});
            skLineSegment(sketch, "E51.9.8", {"start": v(46.72, -22.67) * mm, "end": v(47.75, -22.72) * mm});
            skLineSegment(sketch, "E51.9.9", {"start": v(53.24, -21.75) * mm, "end": v(54.13, -23.1) * mm});
            skLineSegment(sketch, "E51.9.10", {"start": v(51.53, -22.5) * mm, "end": v(53.02, -22.27) * mm});
            skLineSegment(sketch, "E51.9.11", {"start": v(49.82, -17.7) * mm, "end": v(50.63, -18.51) * mm});
            skLineSegment(sketch, "E51.9.12", {"start": v(52.35, -20.53) * mm, "end": v(53.24, -21.75) * mm});
            skLineSegment(sketch, "E51.9.13", {"start": v(44.4, -22.34) * mm, "end": v(45.05, -22.47) * mm});
            skLineSegment(sketch, "E51.9.14", {"start": v(45.05, -22.47) * mm, "end": v(45.82, -22.58) * mm});
            skLineSegment(sketch, "E51.9.15", {"start": v(45.82, -22.58) * mm, "end": v(46.72, -22.67) * mm});
            skLineSegment(sketch, "E51.9.16", {"start": v(48.37, -16.43) * mm, "end": v(49.07, -17) * mm});
            skLineSegment(sketch, "E51.9.17", {"start": v(47.74, -15.96) * mm, "end": v(48.37, -16.43) * mm});
            skLineSegment(sketch, "E51.9.18", {"start": v(49.07, -17) * mm, "end": v(49.82, -17.7) * mm});
            skLineSegment(sketch, "E51.9.19", {"start": v(43.87, -22.2) * mm, "end": v(44.4, -22.34) * mm});
            skLineSegment(sketch, "E51.9.20", {"start": v(43.47, -22.09) * mm, "end": v(43.87, -22.2) * mm});
            skLineSegment(sketch, "E51.9.21", {"start": v(47.2, -15.6) * mm, "end": v(47.74, -15.96) * mm});
            skLineSegment(sketch, "E51.9.22", {"start": v(46.73, -15.32) * mm, "end": v(47.2, -15.6) * mm});
            skLineSegment(sketch, "E51.9.23", {"start": v(46.08, -14.99) * mm, "end": v(46.35, -15.12) * mm});
            skLineSegment(sketch, "E51.9.24", {"start": v(42.96, -21.9) * mm, "end": v(43.02, -21.92) * mm});
            skLineSegment(sketch, "E51.9.25", {"start": v(43.02, -21.92) * mm, "end": v(43.18, -21.99) * mm});
            skLineSegment(sketch, "E51.9.26", {"start": v(46.35, -15.12) * mm, "end": v(46.73, -15.32) * mm});
            skLineSegment(sketch, "E51.9.27", {"start": v(43.18, -21.99) * mm, "end": v(43.47, -22.09) * mm});
            skLineSegment(sketch, "E51.9.28", {"start": v(45.91, -14.92) * mm, "end": v(46.08, -14.99) * mm});
            skLineSegment(sketch, "E51.9.29", {"start": v(45.86, -14.9) * mm, "end": v(45.91, -14.92) * mm});
            skLineSegment(sketch, "E51.10.0", {"start": v(44.04, 0) * mm, "end": v(48.22, 0) * mm});
            skLineSegment(sketch, "E51.10.1", {"start": v(54.7, -6.04) * mm, "end": v(55.96, -5.47) * mm});
            skLineSegment(sketch, "E51.10.2", {"start": v(43.5, -6.89) * mm, "end": v(47.62, -7.54) * mm});
            skLineSegment(sketch, "E51.10.3", {"start": v(53.52, -6.5) * mm, "end": v(54.7, -6.04) * mm});
            skLineSegment(sketch, "E51.10.4", {"start": v(53.87, -1.96) * mm, "end": v(54.97, -2.6) * mm});
            skLineSegment(sketch, "E51.10.5", {"start": v(54.97, -2.6) * mm, "end": v(56.13, -3.35) * mm});
            skLineSegment(sketch, "E51.10.6", {"start": v(52.43, -6.85) * mm, "end": v(53.52, -6.5) * mm});
            skLineSegment(sketch, "E51.10.7", {"start": v(57.3, -4.8) * mm, "end": v(58.72, -3.99) * mm});
            skLineSegment(sketch, "E51.10.8", {"start": v(51.44, -7.12) * mm, "end": v(52.43, -6.85) * mm});
            skLineSegment(sketch, "E51.10.9", {"start": v(57.35, -4.23) * mm, "end": v(58.62, -5.25) * mm});
            skLineSegment(sketch, "E51.10.10", {"start": v(55.96, -5.47) * mm, "end": v(57.3, -4.8) * mm});
            skLineSegment(sketch, "E51.10.11", {"start": v(52.86, -1.44) * mm, "end": v(53.87, -1.96) * mm});
            skLineSegment(sketch, "E51.10.12", {"start": v(56.13, -3.35) * mm, "end": v(57.35, -4.23) * mm});
            skLineSegment(sketch, "E51.10.13", {"start": v(49.13, -7.53) * mm, "end": v(49.79, -7.45) * mm});
            skLineSegment(sketch, "E51.10.14", {"start": v(49.79, -7.45) * mm, "end": v(50.56, -7.32) * mm});
            skLineSegment(sketch, "E51.10.15", {"start": v(50.56, -7.32) * mm, "end": v(51.44, -7.12) * mm});
            skLineSegment(sketch, "E51.10.16", {"start": v(51.08, -0.68) * mm, "end": v(51.92, -1.01) * mm});
            skLineSegment(sketch, "E51.10.17", {"start": v(50.34, -0.43) * mm, "end": v(51.08, -0.68) * mm});
            skLineSegment(sketch, "E51.10.18", {"start": v(51.92, -1.01) * mm, "end": v(52.86, -1.44) * mm});
            skLineSegment(sketch, "E51.10.19", {"start": v(48.59, -7.57) * mm, "end": v(49.13, -7.53) * mm});
            skLineSegment(sketch, "E51.10.20", {"start": v(48.17, -7.57) * mm, "end": v(48.59, -7.57) * mm});
            skLineSegment(sketch, "E51.10.21", {"start": v(49.7, -0.25) * mm, "end": v(50.34, -0.43) * mm});
            skLineSegment(sketch, "E51.10.22", {"start": v(49.17, -0.13) * mm, "end": v(49.7, -0.25) * mm});
            skLineSegment(sketch, "E51.10.23", {"start": v(48.46, -0.02) * mm, "end": v(48.76, -0.05) * mm});
            skLineSegment(sketch, "E51.10.24", {"start": v(47.62, -7.54) * mm, "end": v(47.68, -7.55) * mm});
            skLineSegment(sketch, "E51.10.25", {"start": v(47.68, -7.55) * mm, "end": v(47.86, -7.56) * mm});
            skLineSegment(sketch, "E51.10.26", {"start": v(48.76, -0.05) * mm, "end": v(49.17, -0.13) * mm});
            skLineSegment(sketch, "E51.10.27", {"start": v(47.86, -7.56) * mm, "end": v(48.17, -7.57) * mm});
            skLineSegment(sketch, "E51.10.28", {"start": v(48.28, 0) * mm, "end": v(48.46, -0.02) * mm});
            skLineSegment(sketch, "E51.10.29", {"start": v(48.22, 0) * mm, "end": v(48.28, 0) * mm});
            skLineSegment(sketch, "E51.11.0", {"start": v(41.89, 13.6) * mm, "end": v(45.86, 14.9) * mm});
            skLineSegment(sketch, "E51.11.1", {"start": v(53.89, 11.16) * mm, "end": v(54.92, 12.09) * mm});
            skLineSegment(sketch, "E51.11.2", {"start": v(43.5, 6.89) * mm, "end": v(47.62, 7.54) * mm});
            skLineSegment(sketch, "E51.11.3", {"start": v(52.9, 10.36) * mm, "end": v(53.89, 11.16) * mm});
            skLineSegment(sketch, "E51.11.4", {"start": v(51.84, 14.78) * mm, "end": v(53.08, 14.52) * mm});
            skLineSegment(sketch, "E51.11.5", {"start": v(53.08, 14.52) * mm, "end": v(54.42, 14.16) * mm});
            skLineSegment(sketch, "E51.11.6", {"start": v(51.98, 9.69) * mm, "end": v(52.9, 10.36) * mm});
            skLineSegment(sketch, "E51.11.7", {"start": v(55.98, 13.15) * mm, "end": v(57.08, 14.35) * mm});
            skLineSegment(sketch, "E51.11.8", {"start": v(51.12, 9.12) * mm, "end": v(51.98, 9.69) * mm});
            skLineSegment(sketch, "E51.11.9", {"start": v(55.85, 13.7) * mm, "end": v(57.37, 13.12) * mm});
            skLineSegment(sketch, "E51.11.10", {"start": v(54.92, 12.09) * mm, "end": v(55.98, 13.15) * mm});
            skLineSegment(sketch, "E51.11.11", {"start": v(50.71, 14.97) * mm, "end": v(51.84, 14.78) * mm});
            skLineSegment(sketch, "E51.11.12", {"start": v(54.42, 14.16) * mm, "end": v(55.85, 13.7) * mm});
            skLineSegment(sketch, "E51.11.13", {"start": v(49.05, 8.02) * mm, "end": v(49.65, 8.3) * mm});
            skLineSegment(sketch, "E51.11.14", {"start": v(49.65, 8.3) * mm, "end": v(50.35, 8.66) * mm});
            skLineSegment(sketch, "E51.11.15", {"start": v(50.35, 8.66) * mm, "end": v(51.12, 9.12) * mm});
            skLineSegment(sketch, "E51.11.16", {"start": v(48.8, 15.14) * mm, "end": v(49.7, 15.08) * mm});
            skLineSegment(sketch, "E51.11.17", {"start": v(48, 15.15) * mm, "end": v(48.8, 15.14) * mm});
            skLineSegment(sketch, "E51.11.18", {"start": v(49.7, 15.08) * mm, "end": v(50.71, 14.97) * mm});
            skLineSegment(sketch, "E51.11.19", {"start": v(48.55, 7.82) * mm, "end": v(49.05, 8.02) * mm});
            skLineSegment(sketch, "E51.11.20", {"start": v(48.15, 7.68) * mm, "end": v(48.55, 7.82) * mm});
            skLineSegment(sketch, "E51.11.21", {"start": v(47.35, 15.12) * mm, "end": v(48, 15.15) * mm});
            skLineSegment(sketch, "E51.11.22", {"start": v(46.8, 15.07) * mm, "end": v(47.35, 15.12) * mm});
            skLineSegment(sketch, "E51.11.23", {"start": v(46.1, 14.96) * mm, "end": v(46.39, 15.02) * mm});
            skLineSegment(sketch, "E51.11.24", {"start": v(47.62, 7.54) * mm, "end": v(47.68, 7.55) * mm});
            skLineSegment(sketch, "E51.11.25", {"start": v(47.68, 7.55) * mm, "end": v(47.86, 7.6) * mm});
            skLineSegment(sketch, "E51.11.26", {"start": v(46.39, 15.02) * mm, "end": v(46.8, 15.07) * mm});
            skLineSegment(sketch, "E51.11.27", {"start": v(47.86, 7.6) * mm, "end": v(48.15, 7.68) * mm});
            skLineSegment(sketch, "E51.11.28", {"start": v(45.92, 14.92) * mm, "end": v(46.1, 14.96) * mm});
            skLineSegment(sketch, "E51.11.29", {"start": v(45.86, 14.9) * mm, "end": v(45.92, 14.92) * mm});
            skLineSegment(sketch, "E51.12.0", {"start": v(35.63, 25.89) * mm, "end": v(39, 28.34) * mm});
            skLineSegment(sketch, "E51.12.1", {"start": v(47.8, 27.27) * mm, "end": v(48.5, 28.47) * mm});
            skLineSegment(sketch, "E51.12.2", {"start": v(39.24, 20) * mm, "end": v(42.96, 21.9) * mm});
            skLineSegment(sketch, "E51.12.3", {"start": v(47.11, 26.2) * mm, "end": v(47.8, 27.27) * mm});
            skLineSegment(sketch, "E51.12.4", {"start": v(44.74, 30.08) * mm, "end": v(46, 30.21) * mm});
            skLineSegment(sketch, "E51.12.5", {"start": v(46, 30.21) * mm, "end": v(47.38, 30.28) * mm});
            skLineSegment(sketch, "E51.12.6", {"start": v(46.44, 25.27) * mm, "end": v(47.11, 26.2) * mm});
            skLineSegment(sketch, "E51.12.7", {"start": v(49.18, 29.8) * mm, "end": v(49.85, 31.29) * mm});
            skLineSegment(sketch, "E51.12.8", {"start": v(45.8, 24.47) * mm, "end": v(46.44, 25.27) * mm});
            skLineSegment(sketch, "E51.12.9", {"start": v(48.89, 30.29) * mm, "end": v(50.51, 30.21) * mm});
            skLineSegment(sketch, "E51.12.10", {"start": v(48.5, 28.47) * mm, "end": v(49.18, 29.8) * mm});
            skLineSegment(sketch, "E51.12.11", {"start": v(43.6, 29.9) * mm, "end": v(44.74, 30.08) * mm});
            skLineSegment(sketch, "E51.12.12", {"start": v(47.38, 30.28) * mm, "end": v(48.89, 30.29) * mm});
            skLineSegment(sketch, "E51.12.13", {"start": v(44.17, 22.79) * mm, "end": v(44.66, 23.24) * mm});
            skLineSegment(sketch, "E51.12.14", {"start": v(44.66, 23.24) * mm, "end": v(45.2, 23.8) * mm});
            skLineSegment(sketch, "E51.12.15", {"start": v(45.2, 23.8) * mm, "end": v(45.8, 24.47) * mm});
            skLineSegment(sketch, "E51.12.16", {"start": v(41.73, 29.47) * mm, "end": v(42.6, 29.7) * mm});
            skLineSegment(sketch, "E51.12.17", {"start": v(40.98, 29.24) * mm, "end": v(41.73, 29.47) * mm});
            skLineSegment(sketch, "E51.12.18", {"start": v(42.6, 29.7) * mm, "end": v(43.6, 29.9) * mm});
            skLineSegment(sketch, "E51.12.19", {"start": v(43.75, 22.44) * mm, "end": v(44.17, 22.79) * mm});
            skLineSegment(sketch, "E51.12.20", {"start": v(43.42, 22.18) * mm, "end": v(43.75, 22.44) * mm});
            skLineSegment(sketch, "E51.12.21", {"start": v(40.36, 29.01) * mm, "end": v(40.98, 29.24) * mm});
            skLineSegment(sketch, "E51.12.22", {"start": v(39.86, 28.8) * mm, "end": v(40.36, 29.01) * mm});
            skLineSegment(sketch, "E51.12.23", {"start": v(39.21, 28.47) * mm, "end": v(39.48, 28.61) * mm});
            skLineSegment(sketch, "E51.12.24", {"start": v(42.96, 21.9) * mm, "end": v(43.01, 21.92) * mm});
            skLineSegment(sketch, "E51.12.25", {"start": v(43.01, 21.92) * mm, "end": v(43.17, 22.01) * mm});
            skLineSegment(sketch, "E51.12.26", {"start": v(39.48, 28.61) * mm, "end": v(39.86, 28.8) * mm});
            skLineSegment(sketch, "E51.12.27", {"start": v(43.17, 22.01) * mm, "end": v(43.42, 22.18) * mm});
            skLineSegment(sketch, "E51.12.28", {"start": v(39.06, 28.38) * mm, "end": v(39.21, 28.47) * mm});
            skLineSegment(sketch, "E51.12.29", {"start": v(39, 28.34) * mm, "end": v(39.06, 28.38) * mm});
            skLineSegment(sketch, "E51.13.0", {"start": v(25.89, 35.63) * mm, "end": v(28.34, 39) * mm});
            skLineSegment(sketch, "E51.13.1", {"start": v(37.03, 40.7) * mm, "end": v(37.32, 42.06) * mm});
            skLineSegment(sketch, "E51.13.2", {"start": v(31.14, 31.14) * mm, "end": v(34.1, 34.1) * mm});
            skLineSegment(sketch, "E51.13.3", {"start": v(36.7, 39.48) * mm, "end": v(37.03, 40.7) * mm});
            skLineSegment(sketch, "E51.13.4", {"start": v(33.25, 42.43) * mm, "end": v(34.4, 42.95) * mm});
            skLineSegment(sketch, "E51.13.5", {"start": v(34.4, 42.95) * mm, "end": v(35.7, 43.44) * mm});
            skLineSegment(sketch, "E51.13.6", {"start": v(36.36, 38.39) * mm, "end": v(36.7, 39.48) * mm});
            skLineSegment(sketch, "E51.13.7", {"start": v(37.56, 43.55) * mm, "end": v(37.74, 45.16) * mm});
            skLineSegment(sketch, "E51.13.8", {"start": v(36, 37.43) * mm, "end": v(36.36, 38.39) * mm});
            skLineSegment(sketch, "E51.13.9", {"start": v(37.13, 43.91) * mm, "end": v(38.7, 44.34) * mm});
            skLineSegment(sketch, "E51.13.10", {"start": v(37.32, 42.06) * mm, "end": v(37.56, 43.55) * mm});
            skLineSegment(sketch, "E51.13.11", {"start": v(32.23, 41.92) * mm, "end": v(33.25, 42.43) * mm});
            skLineSegment(sketch, "E51.13.12", {"start": v(35.7, 43.44) * mm, "end": v(37.13, 43.91) * mm});
            skLineSegment(sketch, "E51.13.13", {"start": v(34.97, 35.32) * mm, "end": v(35.3, 35.9) * mm});
            skLineSegment(sketch, "E51.13.14", {"start": v(35.3, 35.9) * mm, "end": v(35.64, 36.6) * mm});
            skLineSegment(sketch, "E51.13.15", {"start": v(35.64, 36.6) * mm, "end": v(36, 37.43) * mm});
            skLineSegment(sketch, "E51.13.16", {"start": v(30.58, 40.93) * mm, "end": v(31.34, 41.41) * mm});
            skLineSegment(sketch, "E51.13.17", {"start": v(29.94, 40.47) * mm, "end": v(30.58, 40.93) * mm});
            skLineSegment(sketch, "E51.13.18", {"start": v(31.34, 41.41) * mm, "end": v(32.23, 41.92) * mm});
            skLineSegment(sketch, "E51.13.19", {"start": v(34.68, 34.86) * mm, "end": v(34.97, 35.32) * mm});
            skLineSegment(sketch, "E51.13.20", {"start": v(34.44, 34.51) * mm, "end": v(34.68, 34.86) * mm});
            skLineSegment(sketch, "E51.13.21", {"start": v(29.42, 40.06) * mm, "end": v(29.94, 40.47) * mm});
            skLineSegment(sketch, "E51.13.22", {"start": v(29, 39.7) * mm, "end": v(29.42, 40.06) * mm});
            skLineSegment(sketch, "E51.13.23", {"start": v(28.5, 39.2) * mm, "end": v(28.7, 39.41) * mm});
            skLineSegment(sketch, "E51.13.24", {"start": v(34.1, 34.1) * mm, "end": v(34.14, 34.14) * mm});
            skLineSegment(sketch, "E51.13.25", {"start": v(34.14, 34.14) * mm, "end": v(34.25, 34.28) * mm});
            skLineSegment(sketch, "E51.13.26", {"start": v(28.7, 39.41) * mm, "end": v(29, 39.7) * mm});
            skLineSegment(sketch, "E51.13.27", {"start": v(34.25, 34.28) * mm, "end": v(34.44, 34.51) * mm});
            skLineSegment(sketch, "E51.13.28", {"start": v(28.38, 39.06) * mm, "end": v(28.5, 39.2) * mm});
            skLineSegment(sketch, "E51.13.29", {"start": v(28.34, 39) * mm, "end": v(28.38, 39.06) * mm});
            skLineSegment(sketch, "E51.14.0", {"start": v(13.6, 41.89) * mm, "end": v(14.9, 45.86) * mm});
            skLineSegment(sketch, "E51.14.1", {"start": v(22.64, 50.15) * mm, "end": v(22.5, 51.53) * mm});
            skLineSegment(sketch, "E51.14.2", {"start": v(20, 39.24) * mm, "end": v(21.9, 42.96) * mm});
            skLineSegment(sketch, "E51.14.3", {"start": v(22.71, 48.9) * mm, "end": v(22.64, 50.15) * mm});
            skLineSegment(sketch, "E51.14.4", {"start": v(18.51, 50.63) * mm, "end": v(19.45, 51.48) * mm});
            skLineSegment(sketch, "E51.14.5", {"start": v(19.45, 51.48) * mm, "end": v(20.53, 52.35) * mm});
            skLineSegment(sketch, "E51.14.6", {"start": v(22.72, 47.75) * mm, "end": v(22.71, 48.9) * mm});
            skLineSegment(sketch, "E51.14.7", {"start": v(22.27, 53.02) * mm, "end": v(21.94, 54.62) * mm});
            skLineSegment(sketch, "E51.14.8", {"start": v(22.67, 46.72) * mm, "end": v(22.72, 47.75) * mm});
            skLineSegment(sketch, "E51.14.9", {"start": v(21.75, 53.24) * mm, "end": v(23.1, 54.13) * mm});
            skLineSegment(sketch, "E51.14.10", {"start": v(22.5, 51.53) * mm, "end": v(22.27, 53.02) * mm});
            skLineSegment(sketch, "E51.14.11", {"start": v(17.7, 49.82) * mm, "end": v(18.51, 50.63) * mm});
            skLineSegment(sketch, "E51.14.12", {"start": v(20.53, 52.35) * mm, "end": v(21.75, 53.24) * mm});
            skLineSegment(sketch, "E51.14.13", {"start": v(22.34, 44.4) * mm, "end": v(22.47, 45.05) * mm});
            skLineSegment(sketch, "E51.14.14", {"start": v(22.47, 45.05) * mm, "end": v(22.58, 45.82) * mm});
            skLineSegment(sketch, "E51.14.15", {"start": v(22.58, 45.82) * mm, "end": v(22.67, 46.72) * mm});
            skLineSegment(sketch, "E51.14.16", {"start": v(16.43, 48.37) * mm, "end": v(17, 49.07) * mm});
            skLineSegment(sketch, "E51.14.17", {"start": v(15.96, 47.74) * mm, "end": v(16.43, 48.37) * mm});
            skLineSegment(sketch, "E51.14.18", {"start": v(17, 49.07) * mm, "end": v(17.7, 49.82) * mm});
            skLineSegment(sketch, "E51.14.19", {"start": v(22.2, 43.87) * mm, "end": v(22.34, 44.4) * mm});
            skLineSegment(sketch, "E51.14.20", {"start": v(22.09, 43.47) * mm, "end": v(22.2, 43.87) * mm});
            skLineSegment(sketch, "E51.14.21", {"start": v(15.6, 47.2) * mm, "end": v(15.96, 47.74) * mm});
            skLineSegment(sketch, "E51.14.22", {"start": v(15.32, 46.73) * mm, "end": v(15.6, 47.2) * mm});
            skLineSegment(sketch, "E51.14.23", {"start": v(14.99, 46.08) * mm, "end": v(15.12, 46.35) * mm});
            skLineSegment(sketch, "E51.14.24", {"start": v(21.9, 42.96) * mm, "end": v(21.92, 43.02) * mm});
            skLineSegment(sketch, "E51.14.25", {"start": v(21.92, 43.02) * mm, "end": v(21.99, 43.18) * mm});
            skLineSegment(sketch, "E51.14.26", {"start": v(15.12, 46.35) * mm, "end": v(15.32, 46.73) * mm});
            skLineSegment(sketch, "E51.14.27", {"start": v(21.99, 43.18) * mm, "end": v(22.09, 43.47) * mm});
            skLineSegment(sketch, "E51.14.28", {"start": v(14.92, 45.91) * mm, "end": v(14.99, 46.08) * mm});
            skLineSegment(sketch, "E51.14.29", {"start": v(14.9, 45.86) * mm, "end": v(14.92, 45.91) * mm});
            skLineSegment(sketch, "E51.15.0", {"start": v(0, 44.04) * mm, "end": v(0, 48.22) * mm});
            skLineSegment(sketch, "E51.15.1", {"start": v(6.04, 54.7) * mm, "end": v(5.47, 55.96) * mm});
            skLineSegment(sketch, "E51.15.2", {"start": v(6.89, 43.5) * mm, "end": v(7.54, 47.62) * mm});
            skLineSegment(sketch, "E51.15.3", {"start": v(6.5, 53.52) * mm, "end": v(6.04, 54.7) * mm});
            skLineSegment(sketch, "E51.15.4", {"start": v(1.96, 53.87) * mm, "end": v(2.6, 54.97) * mm});
            skLineSegment(sketch, "E51.15.5", {"start": v(2.6, 54.97) * mm, "end": v(3.35, 56.13) * mm});
            skLineSegment(sketch, "E51.15.6", {"start": v(6.85, 52.43) * mm, "end": v(6.5, 53.52) * mm});
            skLineSegment(sketch, "E51.15.7", {"start": v(4.8, 57.3) * mm, "end": v(3.99, 58.72) * mm});
            skLineSegment(sketch, "E51.15.8", {"start": v(7.12, 51.44) * mm, "end": v(6.85, 52.43) * mm});
            skLineSegment(sketch, "E51.15.9", {"start": v(4.23, 57.35) * mm, "end": v(5.25, 58.62) * mm});
            skLineSegment(sketch, "E51.15.10", {"start": v(5.47, 55.96) * mm, "end": v(4.8, 57.3) * mm});
            skLineSegment(sketch, "E51.15.11", {"start": v(1.44, 52.86) * mm, "end": v(1.96, 53.87) * mm});
            skLineSegment(sketch, "E51.15.12", {"start": v(3.35, 56.13) * mm, "end": v(4.23, 57.35) * mm});
            skLineSegment(sketch, "E51.15.13", {"start": v(7.53, 49.13) * mm, "end": v(7.45, 49.79) * mm});
            skLineSegment(sketch, "E51.15.14", {"start": v(7.45, 49.79) * mm, "end": v(7.32, 50.56) * mm});
            skLineSegment(sketch, "E51.15.15", {"start": v(7.32, 50.56) * mm, "end": v(7.12, 51.44) * mm});
            skLineSegment(sketch, "E51.15.16", {"start": v(0.68, 51.08) * mm, "end": v(1.01, 51.92) * mm});
            skLineSegment(sketch, "E51.15.17", {"start": v(0.43, 50.34) * mm, "end": v(0.68, 51.08) * mm});
            skLineSegment(sketch, "E51.15.18", {"start": v(1.01, 51.92) * mm, "end": v(1.44, 52.86) * mm});
            skLineSegment(sketch, "E51.15.19", {"start": v(7.57, 48.59) * mm, "end": v(7.53, 49.13) * mm});
            skLineSegment(sketch, "E51.15.20", {"start": v(7.57, 48.17) * mm, "end": v(7.57, 48.59) * mm});
            skLineSegment(sketch, "E51.15.21", {"start": v(0.25, 49.7) * mm, "end": v(0.43, 50.34) * mm});
            skLineSegment(sketch, "E51.15.22", {"start": v(0.13, 49.17) * mm, "end": v(0.25, 49.7) * mm});
            skLineSegment(sketch, "E51.15.23", {"start": v(0.02, 48.46) * mm, "end": v(0.05, 48.76) * mm});
            skLineSegment(sketch, "E51.15.24", {"start": v(7.54, 47.62) * mm, "end": v(7.55, 47.68) * mm});
            skLineSegment(sketch, "E51.15.25", {"start": v(7.55, 47.68) * mm, "end": v(7.56, 47.86) * mm});
            skLineSegment(sketch, "E51.15.26", {"start": v(0.05, 48.76) * mm, "end": v(0.13, 49.17) * mm});
            skLineSegment(sketch, "E51.15.27", {"start": v(7.56, 47.86) * mm, "end": v(7.57, 48.17) * mm});
            skLineSegment(sketch, "E51.15.28", {"start": v(0, 48.28) * mm, "end": v(0.02, 48.46) * mm});
            skLineSegment(sketch, "E51.15.29", {"start": v(0, 48.22) * mm, "end": v(0, 48.28) * mm});
            skLineSegment(sketch, "E51.16.0", {"start": v(-13.6, 41.89) * mm, "end": v(-14.9, 45.86) * mm});
            skLineSegment(sketch, "E51.16.1", {"start": v(-11.16, 53.89) * mm, "end": v(-12.09, 54.92) * mm});
            skLineSegment(sketch, "E51.16.2", {"start": v(-6.89, 43.5) * mm, "end": v(-7.54, 47.62) * mm});
            skLineSegment(sketch, "E51.16.3", {"start": v(-10.36, 52.9) * mm, "end": v(-11.16, 53.89) * mm});
            skLineSegment(sketch, "E51.16.4", {"start": v(-14.78, 51.84) * mm, "end": v(-14.52, 53.08) * mm});
            skLineSegment(sketch, "E51.16.5", {"start": v(-14.52, 53.08) * mm, "end": v(-14.16, 54.42) * mm});
            skLineSegment(sketch, "E51.16.6", {"start": v(-9.69, 51.98) * mm, "end": v(-10.36, 52.9) * mm});
            skLineSegment(sketch, "E51.16.7", {"start": v(-13.15, 55.98) * mm, "end": v(-14.35, 57.08) * mm});
            skLineSegment(sketch, "E51.16.8", {"start": v(-9.12, 51.12) * mm, "end": v(-9.69, 51.98) * mm});
            skLineSegment(sketch, "E51.16.9", {"start": v(-13.7, 55.85) * mm, "end": v(-13.12, 57.37) * mm});
            skLineSegment(sketch, "E51.16.10", {"start": v(-12.09, 54.92) * mm, "end": v(-13.15, 55.98) * mm});
            skLineSegment(sketch, "E51.16.11", {"start": v(-14.97, 50.71) * mm, "end": v(-14.78, 51.84) * mm});
            skLineSegment(sketch, "E51.16.12", {"start": v(-14.16, 54.42) * mm, "end": v(-13.7, 55.85) * mm});
            skLineSegment(sketch, "E51.16.13", {"start": v(-8.02, 49.05) * mm, "end": v(-8.3, 49.65) * mm});
            skLineSegment(sketch, "E51.16.14", {"start": v(-8.3, 49.65) * mm, "end": v(-8.66, 50.35) * mm});
            skLineSegment(sketch, "E51.16.15", {"start": v(-8.66, 50.35) * mm, "end": v(-9.12, 51.12) * mm});
            skLineSegment(sketch, "E51.16.16", {"start": v(-15.14, 48.8) * mm, "end": v(-15.08, 49.7) * mm});
            skLineSegment(sketch, "E51.16.17", {"start": v(-15.15, 48) * mm, "end": v(-15.14, 48.8) * mm});
            skLineSegment(sketch, "E51.16.18", {"start": v(-15.08, 49.7) * mm, "end": v(-14.97, 50.71) * mm});
            skLineSegment(sketch, "E51.16.19", {"start": v(-7.82, 48.55) * mm, "end": v(-8.02, 49.05) * mm});
            skLineSegment(sketch, "E51.16.20", {"start": v(-7.68, 48.15) * mm, "end": v(-7.82, 48.55) * mm});
            skLineSegment(sketch, "E51.16.21", {"start": v(-15.12, 47.35) * mm, "end": v(-15.15, 48) * mm});
            skLineSegment(sketch, "E51.16.22", {"start": v(-15.07, 46.8) * mm, "end": v(-15.12, 47.35) * mm});
            skLineSegment(sketch, "E51.16.23", {"start": v(-14.96, 46.1) * mm, "end": v(-15.02, 46.39) * mm});
            skLineSegment(sketch, "E51.16.24", {"start": v(-7.54, 47.62) * mm, "end": v(-7.55, 47.68) * mm});
            skLineSegment(sketch, "E51.16.25", {"start": v(-7.55, 47.68) * mm, "end": v(-7.6, 47.86) * mm});
            skLineSegment(sketch, "E51.16.26", {"start": v(-15.02, 46.39) * mm, "end": v(-15.07, 46.8) * mm});
            skLineSegment(sketch, "E51.16.27", {"start": v(-7.6, 47.86) * mm, "end": v(-7.68, 48.15) * mm});
            skLineSegment(sketch, "E51.16.28", {"start": v(-14.92, 45.92) * mm, "end": v(-14.96, 46.1) * mm});
            skLineSegment(sketch, "E51.16.29", {"start": v(-14.9, 45.86) * mm, "end": v(-14.92, 45.92) * mm});
            skLineSegment(sketch, "E51.17.0", {"start": v(-25.89, 35.63) * mm, "end": v(-28.34, 39) * mm});
            skLineSegment(sketch, "E51.17.1", {"start": v(-27.27, 47.8) * mm, "end": v(-28.47, 48.5) * mm});
            skLineSegment(sketch, "E51.17.2", {"start": v(-20, 39.24) * mm, "end": v(-21.9, 42.96) * mm});
            skLineSegment(sketch, "E51.17.3", {"start": v(-26.2, 47.11) * mm, "end": v(-27.27, 47.8) * mm});
            skLineSegment(sketch, "E51.17.4", {"start": v(-30.08, 44.74) * mm, "end": v(-30.21, 46) * mm});
            skLineSegment(sketch, "E51.17.5", {"start": v(-30.21, 46) * mm, "end": v(-30.28, 47.38) * mm});
            skLineSegment(sketch, "E51.17.6", {"start": v(-25.27, 46.44) * mm, "end": v(-26.2, 47.11) * mm});
            skLineSegment(sketch, "E51.17.7", {"start": v(-29.8, 49.18) * mm, "end": v(-31.29, 49.85) * mm});
            skLineSegment(sketch, "E51.17.8", {"start": v(-24.47, 45.8) * mm, "end": v(-25.27, 46.44) * mm});
            skLineSegment(sketch, "E51.17.9", {"start": v(-30.29, 48.89) * mm, "end": v(-30.21, 50.51) * mm});
            skLineSegment(sketch, "E51.17.10", {"start": v(-28.47, 48.5) * mm, "end": v(-29.8, 49.18) * mm});
            skLineSegment(sketch, "E51.17.11", {"start": v(-29.9, 43.6) * mm, "end": v(-30.08, 44.74) * mm});
            skLineSegment(sketch, "E51.17.12", {"start": v(-30.28, 47.38) * mm, "end": v(-30.29, 48.89) * mm});
            skLineSegment(sketch, "E51.17.13", {"start": v(-22.79, 44.17) * mm, "end": v(-23.24, 44.66) * mm});
            skLineSegment(sketch, "E51.17.14", {"start": v(-23.24, 44.66) * mm, "end": v(-23.8, 45.2) * mm});
            skLineSegment(sketch, "E51.17.15", {"start": v(-23.8, 45.2) * mm, "end": v(-24.47, 45.8) * mm});
            skLineSegment(sketch, "E51.17.16", {"start": v(-29.47, 41.73) * mm, "end": v(-29.7, 42.6) * mm});
            skLineSegment(sketch, "E51.17.17", {"start": v(-29.24, 40.98) * mm, "end": v(-29.47, 41.73) * mm});
            skLineSegment(sketch, "E51.17.18", {"start": v(-29.7, 42.6) * mm, "end": v(-29.9, 43.6) * mm});
            skLineSegment(sketch, "E51.17.19", {"start": v(-22.44, 43.75) * mm, "end": v(-22.79, 44.17) * mm});
            skLineSegment(sketch, "E51.17.20", {"start": v(-22.18, 43.42) * mm, "end": v(-22.44, 43.75) * mm});
            skLineSegment(sketch, "E51.17.21", {"start": v(-29.01, 40.36) * mm, "end": v(-29.24, 40.98) * mm});
            skLineSegment(sketch, "E51.17.22", {"start": v(-28.8, 39.86) * mm, "end": v(-29.01, 40.36) * mm});
            skLineSegment(sketch, "E51.17.23", {"start": v(-28.47, 39.21) * mm, "end": v(-28.61, 39.48) * mm});
            skLineSegment(sketch, "E51.17.24", {"start": v(-21.9, 42.96) * mm, "end": v(-21.92, 43.01) * mm});
            skLineSegment(sketch, "E51.17.25", {"start": v(-21.92, 43.01) * mm, "end": v(-22.01, 43.17) * mm});
            skLineSegment(sketch, "E51.17.26", {"start": v(-28.61, 39.48) * mm, "end": v(-28.8, 39.86) * mm});
            skLineSegment(sketch, "E51.17.27", {"start": v(-22.01, 43.17) * mm, "end": v(-22.18, 43.42) * mm});
            skLineSegment(sketch, "E51.17.28", {"start": v(-28.38, 39.06) * mm, "end": v(-28.47, 39.21) * mm});
            skLineSegment(sketch, "E51.17.29", {"start": v(-28.34, 39) * mm, "end": v(-28.38, 39.06) * mm});
            skLineSegment(sketch, "E51.18.0", {"start": v(-35.63, 25.89) * mm, "end": v(-39, 28.34) * mm});
            skLineSegment(sketch, "E51.18.1", {"start": v(-40.7, 37.03) * mm, "end": v(-42.06, 37.32) * mm});
            skLineSegment(sketch, "E51.18.2", {"start": v(-31.14, 31.14) * mm, "end": v(-34.1, 34.1) * mm});
            skLineSegment(sketch, "E51.18.3", {"start": v(-39.48, 36.7) * mm, "end": v(-40.7, 37.03) * mm});
            skLineSegment(sketch, "E51.18.4", {"start": v(-42.43, 33.25) * mm, "end": v(-42.95, 34.4) * mm});
            skLineSegment(sketch, "E51.18.5", {"start": v(-42.95, 34.4) * mm, "end": v(-43.44, 35.7) * mm});
            skLineSegment(sketch, "E51.18.6", {"start": v(-38.39, 36.36) * mm, "end": v(-39.48, 36.7) * mm});
            skLineSegment(sketch, "E51.18.7", {"start": v(-43.55, 37.56) * mm, "end": v(-45.16, 37.74) * mm});
            skLineSegment(sketch, "E51.18.8", {"start": v(-37.43, 36) * mm, "end": v(-38.39, 36.36) * mm});
            skLineSegment(sketch, "E51.18.9", {"start": v(-43.91, 37.13) * mm, "end": v(-44.34, 38.7) * mm});
            skLineSegment(sketch, "E51.18.10", {"start": v(-42.06, 37.32) * mm, "end": v(-43.55, 37.56) * mm});
            skLineSegment(sketch, "E51.18.11", {"start": v(-41.92, 32.23) * mm, "end": v(-42.43, 33.25) * mm});
            skLineSegment(sketch, "E51.18.12", {"start": v(-43.44, 35.7) * mm, "end": v(-43.91, 37.13) * mm});
            skLineSegment(sketch, "E51.18.13", {"start": v(-35.32, 34.97) * mm, "end": v(-35.9, 35.3) * mm});
            skLineSegment(sketch, "E51.18.14", {"start": v(-35.9, 35.3) * mm, "end": v(-36.6, 35.64) * mm});
            skLineSegment(sketch, "E51.18.15", {"start": v(-36.6, 35.64) * mm, "end": v(-37.43, 36) * mm});
            skLineSegment(sketch, "E51.18.16", {"start": v(-40.93, 30.58) * mm, "end": v(-41.41, 31.34) * mm});
            skLineSegment(sketch, "E51.18.17", {"start": v(-40.47, 29.94) * mm, "end": v(-40.93, 30.58) * mm});
            skLineSegment(sketch, "E51.18.18", {"start": v(-41.41, 31.34) * mm, "end": v(-41.92, 32.23) * mm});
            skLineSegment(sketch, "E51.18.19", {"start": v(-34.86, 34.68) * mm, "end": v(-35.32, 34.97) * mm});
            skLineSegment(sketch, "E51.18.20", {"start": v(-34.51, 34.44) * mm, "end": v(-34.86, 34.68) * mm});
            skLineSegment(sketch, "E51.18.21", {"start": v(-40.06, 29.42) * mm, "end": v(-40.47, 29.94) * mm});
            skLineSegment(sketch, "E51.18.22", {"start": v(-39.7, 29) * mm, "end": v(-40.06, 29.42) * mm});
            skLineSegment(sketch, "E51.18.23", {"start": v(-39.2, 28.5) * mm, "end": v(-39.41, 28.7) * mm});
            skLineSegment(sketch, "E51.18.24", {"start": v(-34.1, 34.1) * mm, "end": v(-34.14, 34.14) * mm});
            skLineSegment(sketch, "E51.18.25", {"start": v(-34.14, 34.14) * mm, "end": v(-34.28, 34.25) * mm});
            skLineSegment(sketch, "E51.18.26", {"start": v(-39.41, 28.7) * mm, "end": v(-39.7, 29) * mm});
            skLineSegment(sketch, "E51.18.27", {"start": v(-34.28, 34.25) * mm, "end": v(-34.51, 34.44) * mm});
            skLineSegment(sketch, "E51.18.28", {"start": v(-39.06, 28.38) * mm, "end": v(-39.2, 28.5) * mm});
            skLineSegment(sketch, "E51.18.29", {"start": v(-39, 28.34) * mm, "end": v(-39.06, 28.38) * mm});
            skLineSegment(sketch, "E51.19.0", {"start": v(-41.89, 13.6) * mm, "end": v(-45.86, 14.9) * mm});
            skLineSegment(sketch, "E51.19.1", {"start": v(-50.15, 22.64) * mm, "end": v(-51.53, 22.5) * mm});
            skLineSegment(sketch, "E51.19.2", {"start": v(-39.24, 20) * mm, "end": v(-42.96, 21.9) * mm});
            skLineSegment(sketch, "E51.19.3", {"start": v(-48.9, 22.71) * mm, "end": v(-50.15, 22.64) * mm});
            skLineSegment(sketch, "E51.19.4", {"start": v(-50.63, 18.51) * mm, "end": v(-51.48, 19.45) * mm});
            skLineSegment(sketch, "E51.19.5", {"start": v(-51.48, 19.45) * mm, "end": v(-52.35, 20.53) * mm});
            skLineSegment(sketch, "E51.19.6", {"start": v(-47.75, 22.72) * mm, "end": v(-48.9, 22.71) * mm});
            skLineSegment(sketch, "E51.19.7", {"start": v(-53.02, 22.27) * mm, "end": v(-54.62, 21.94) * mm});
            skLineSegment(sketch, "E51.19.8", {"start": v(-46.72, 22.67) * mm, "end": v(-47.75, 22.72) * mm});
            skLineSegment(sketch, "E51.19.9", {"start": v(-53.24, 21.75) * mm, "end": v(-54.13, 23.1) * mm});
            skLineSegment(sketch, "E51.19.10", {"start": v(-51.53, 22.5) * mm, "end": v(-53.02, 22.27) * mm});
            skLineSegment(sketch, "E51.19.11", {"start": v(-49.82, 17.7) * mm, "end": v(-50.63, 18.51) * mm});
            skLineSegment(sketch, "E51.19.12", {"start": v(-52.35, 20.53) * mm, "end": v(-53.24, 21.75) * mm});
            skLineSegment(sketch, "E51.19.13", {"start": v(-44.4, 22.34) * mm, "end": v(-45.05, 22.47) * mm});
            skLineSegment(sketch, "E51.19.14", {"start": v(-45.05, 22.47) * mm, "end": v(-45.82, 22.58) * mm});
            skLineSegment(sketch, "E51.19.15", {"start": v(-45.82, 22.58) * mm, "end": v(-46.72, 22.67) * mm});
            skLineSegment(sketch, "E51.19.16", {"start": v(-48.37, 16.43) * mm, "end": v(-49.07, 17) * mm});
            skLineSegment(sketch, "E51.19.17", {"start": v(-47.74, 15.96) * mm, "end": v(-48.37, 16.43) * mm});
            skLineSegment(sketch, "E51.19.18", {"start": v(-49.07, 17) * mm, "end": v(-49.82, 17.7) * mm});
            skLineSegment(sketch, "E51.19.19", {"start": v(-43.87, 22.2) * mm, "end": v(-44.4, 22.34) * mm});
            skLineSegment(sketch, "E51.19.20", {"start": v(-43.47, 22.09) * mm, "end": v(-43.87, 22.2) * mm});
            skLineSegment(sketch, "E51.19.21", {"start": v(-47.2, 15.6) * mm, "end": v(-47.74, 15.96) * mm});
            skLineSegment(sketch, "E51.19.22", {"start": v(-46.73, 15.32) * mm, "end": v(-47.2, 15.6) * mm});
            skLineSegment(sketch, "E51.19.23", {"start": v(-46.08, 14.99) * mm, "end": v(-46.35, 15.12) * mm});
            skLineSegment(sketch, "E51.19.24", {"start": v(-42.96, 21.9) * mm, "end": v(-43.02, 21.92) * mm});
            skLineSegment(sketch, "E51.19.25", {"start": v(-43.02, 21.92) * mm, "end": v(-43.18, 21.99) * mm});
            skLineSegment(sketch, "E51.19.26", {"start": v(-46.35, 15.12) * mm, "end": v(-46.73, 15.32) * mm});
            skLineSegment(sketch, "E51.19.27", {"start": v(-43.18, 21.99) * mm, "end": v(-43.47, 22.09) * mm});
            skLineSegment(sketch, "E51.19.28", {"start": v(-45.91, 14.92) * mm, "end": v(-46.08, 14.99) * mm});
            skLineSegment(sketch, "E51.19.29", {"start": v(-45.86, 14.9) * mm, "end": v(-45.91, 14.92) * mm});
            skSolve(sketch);
        }
        {
            var Q0;
            {var subQ0=sQuery(id+"F1.wireOp",EDGE,"E0");var subQ27=makeQuery(id+"F1.imprint","INTERSECT",VERTEX,{"derivedFrom":[subQ0,sQuery(id+"F1.wireOp",EDGE,"E51.10.0")]});Q0=makeQuery(id+"F1.imprint","IMPRINT",FACE,{"disambiguationData":[TD([[makeQuery(id+"F1.imprint","IMPRINT",EDGE,{"disambiguationData":[TD([[subQ27,-1.0]])],"derivedFrom":subQ0}),1.0]])]});}
            var Q1;
            {var subQ0=sQuery(id+"F1.wireOp",EDGE,"E51.1.0");Q1=makeQuery(id+"F1.imprint","IMPRINT",FACE,{"disambiguationData":[TD([[makeQuery(id+"F1.imprint","IMPRINT",EDGE,{"derivedFrom":subQ0}),-1.0]])]});}
            var Q2;
            {var subQ7=sQuery(id+"F1.wireOp",EDGE,"E51.2.0");Q2=makeQuery(id+"F1.imprint","IMPRINT",FACE,{"disambiguationData":[TD([[makeQuery(id+"F1.imprint","IMPRINT",EDGE,{"derivedFrom":subQ7}),-1.0]])]});}
            var Q3;
            {var subQ8=sQuery(id+"F1.wireOp",EDGE,"E51.3.0");Q3=makeQuery(id+"F1.imprint","IMPRINT",FACE,{"disambiguationData":[TD([[makeQuery(id+"F1.imprint","IMPRINT",EDGE,{"derivedFrom":subQ8}),-1.0]])]});}
            var Q4;
            {var subQ2=sQuery(id+"F1.wireOp",EDGE,"E51.4.0");Q4=makeQuery(id+"F1.imprint","IMPRINT",FACE,{"disambiguationData":[TD([[makeQuery(id+"F1.imprint","IMPRINT",EDGE,{"derivedFrom":subQ2}),-1.0]])]});}
            var Q5;
            {var subQ8=sQuery(id+"F1.wireOp",EDGE,"E51.5.0");Q5=makeQuery(id+"F1.imprint","IMPRINT",FACE,{"disambiguationData":[TD([[makeQuery(id+"F1.imprint","IMPRINT",EDGE,{"derivedFrom":subQ8}),-1.0]])]});}
            var Q6;
            {var subQ3=sQuery(id+"F1.wireOp",EDGE,"E51.6.0");Q6=makeQuery(id+"F1.imprint","IMPRINT",FACE,{"disambiguationData":[TD([[makeQuery(id+"F1.imprint","IMPRINT",EDGE,{"derivedFrom":subQ3}),-1.0]])]});}
            var Q7;
            {var subQ0=sQuery(id+"F1.wireOp",EDGE,"E51.7.0");Q7=makeQuery(id+"F1.imprint","IMPRINT",FACE,{"disambiguationData":[TD([[makeQuery(id+"F1.imprint","IMPRINT",EDGE,{"derivedFrom":subQ0}),-1.0]])]});}
            var Q8;
            {var subQ5=sQuery(id+"F1.wireOp",EDGE,"E51.8.0");Q8=makeQuery(id+"F1.imprint","IMPRINT",FACE,{"disambiguationData":[TD([[makeQuery(id+"F1.imprint","IMPRINT",EDGE,{"derivedFrom":subQ5}),-1.0]])]});}
            var Q9;
            {var subQ1=sQuery(id+"F1.wireOp",EDGE,"E51.9.0");Q9=makeQuery(id+"F1.imprint","IMPRINT",FACE,{"disambiguationData":[TD([[makeQuery(id+"F1.imprint","IMPRINT",EDGE,{"derivedFrom":subQ1}),-1.0]])]});}
            var Q10;
            {var subQ5=sQuery(id+"F1.wireOp",EDGE,"E51.10.0");Q10=makeQuery(id+"F1.imprint","IMPRINT",FACE,{"disambiguationData":[TD([[makeQuery(id+"F1.imprint","IMPRINT",EDGE,{"derivedFrom":subQ5}),-1.0]])]});}
            var Q11;
            {var subQ8=sQuery(id+"F1.wireOp",EDGE,"E51.11.0");Q11=makeQuery(id+"F1.imprint","IMPRINT",FACE,{"disambiguationData":[TD([[makeQuery(id+"F1.imprint","IMPRINT",EDGE,{"derivedFrom":subQ8}),-1.0]])]});}
            var Q12;
            {var subQ2=sQuery(id+"F1.wireOp",EDGE,"E51.12.0");Q12=makeQuery(id+"F1.imprint","IMPRINT",FACE,{"disambiguationData":[TD([[makeQuery(id+"F1.imprint","IMPRINT",EDGE,{"derivedFrom":subQ2}),-1.0]])]});}
            var Q13;
            {var subQ3=sQuery(id+"F1.wireOp",EDGE,"E51.13.0");Q13=makeQuery(id+"F1.imprint","IMPRINT",FACE,{"disambiguationData":[TD([[makeQuery(id+"F1.imprint","IMPRINT",EDGE,{"derivedFrom":subQ3}),-1.0]])]});}
            var Q14;
            {var subQ0=sQuery(id+"F1.wireOp",EDGE,"E51.14.0");Q14=makeQuery(id+"F1.imprint","IMPRINT",FACE,{"disambiguationData":[TD([[makeQuery(id+"F1.imprint","IMPRINT",EDGE,{"derivedFrom":subQ0}),-1.0]])]});}
            var Q15;
            {var subQ6=sQuery(id+"F1.wireOp",EDGE,"E51.15.0");Q15=makeQuery(id+"F1.imprint","IMPRINT",FACE,{"disambiguationData":[TD([[makeQuery(id+"F1.imprint","IMPRINT",EDGE,{"derivedFrom":subQ6}),-1.0]])]});}
            var Q16;
            {var subQ5=sQuery(id+"F1.wireOp",EDGE,"E51.16.0");Q16=makeQuery(id+"F1.imprint","IMPRINT",FACE,{"disambiguationData":[TD([[makeQuery(id+"F1.imprint","IMPRINT",EDGE,{"derivedFrom":subQ5}),-1.0]])]});}
            var Q17;
            {var subQ7=sQuery(id+"F1.wireOp",EDGE,"E51.17.0");Q17=makeQuery(id+"F1.imprint","IMPRINT",FACE,{"disambiguationData":[TD([[makeQuery(id+"F1.imprint","IMPRINT",EDGE,{"derivedFrom":subQ7}),-1.0]])]});}
            var Q18;
            {var subQ5=sQuery(id+"F1.wireOp",EDGE,"E51.18.0");Q18=makeQuery(id+"F1.imprint","IMPRINT",FACE,{"disambiguationData":[TD([[makeQuery(id+"F1.imprint","IMPRINT",EDGE,{"derivedFrom":subQ5}),-1.0]])]});}
            var Q19;
            {var subQ8=sQuery(id+"F1.wireOp",EDGE,"E51.19.0");Q19=makeQuery(id+"F1.imprint","IMPRINT",FACE,{"disambiguationData":[TD([[makeQuery(id+"F1.imprint","IMPRINT",EDGE,{"derivedFrom":subQ8}),-1.0]])]});}
            var Q20;
            {var subQ8=sQuery(id+"F1.wireOp",EDGE,"E21");Q20=makeQuery(id+"F1.imprint","IMPRINT",FACE,{"disambiguationData":[TD([[makeQuery(id+"F1.imprint","IMPRINT",EDGE,{"derivedFrom":subQ8}),-1.0]])]});}
            extrude(context, id + "F2", {"entities" : qUnion([Q0, Q1, Q2, Q3, Q4, Q5, Q6, Q7, Q8, Q9, Q10, Q11, Q12, Q13, Q14, Q15, Q16, Q17, Q18, Q19, Q20]), "depth" : (getVariable(context, 'GearThickness')) * mm});
        }
    });
